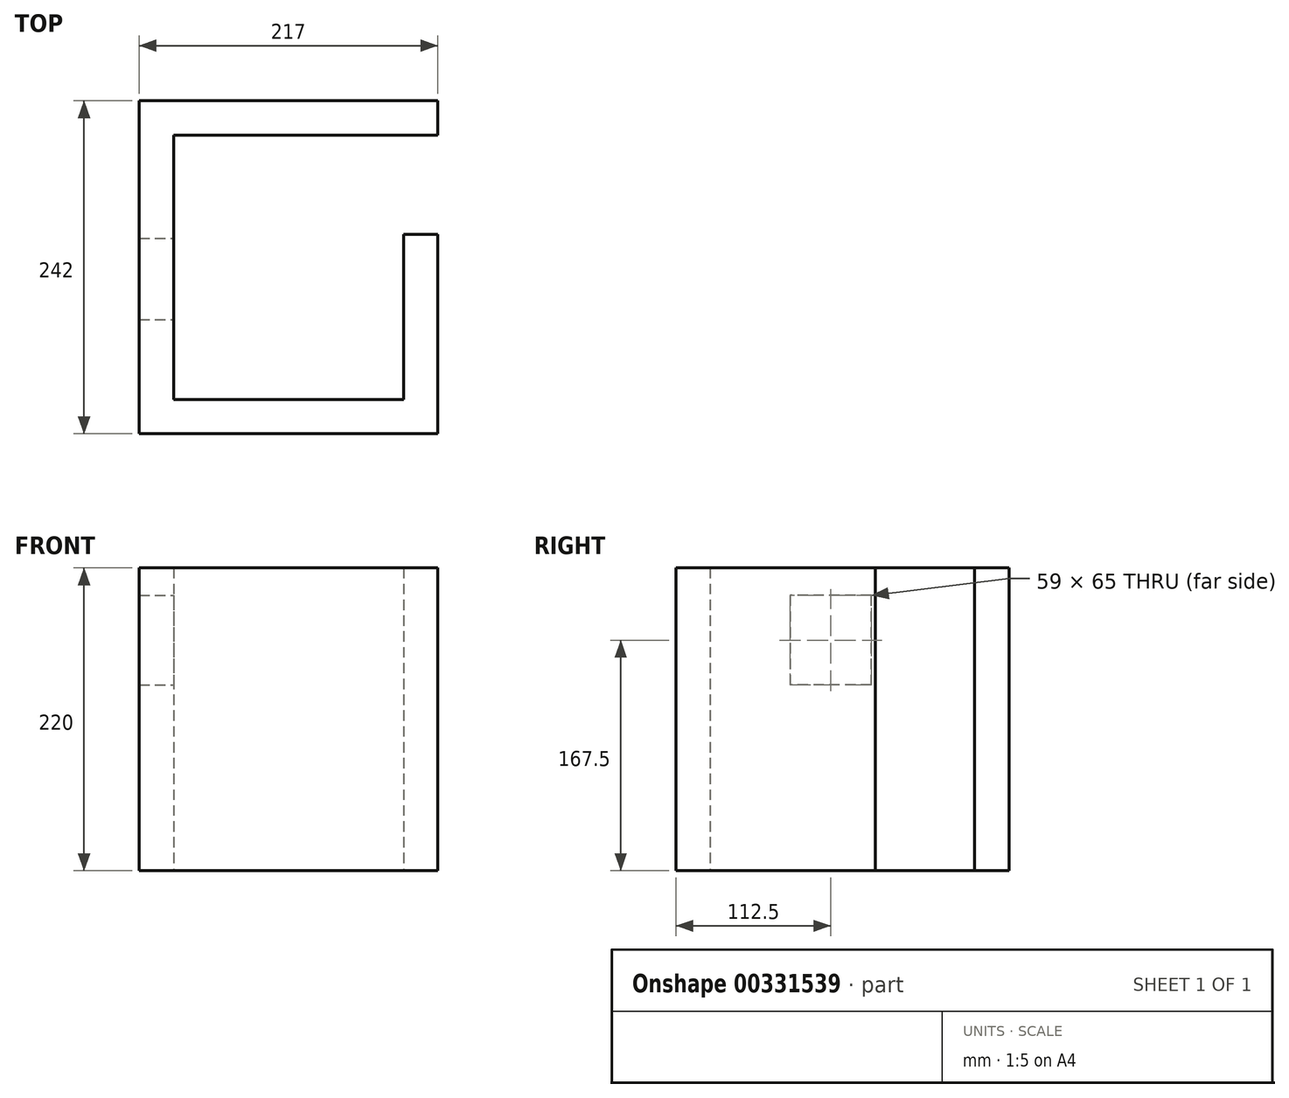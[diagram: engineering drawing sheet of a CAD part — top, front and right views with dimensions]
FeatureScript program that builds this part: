
annotation { "Feature Type Name" : "Feature", "Feature Type Description" : "" }
export const myFeature = defineFeature(function(context is Context, id is Id, definition is map)
    precondition{}
    {
        {
            var Q0;
            Q0=qCreatedBy(makeId("Top.planeOp"),FACE);
            var sketch = newSketch(context, id + "F0", { "sketchPlane" : qUnion([Q0])});
            skLineSegment(sketch, "E0", {"start": v(1313, 440) * mm, "end": v(1313, 406) * mm});
            skLineSegment(sketch, "E1", {"start": v(1313, -267) * mm, "end": v(1313, -301) * mm});
            skLineSegment(sketch, "E2", {"start": v(1313, -301) * mm, "end": v(647, -301) * mm});
            skLineSegment(sketch, "E3", {"start": v(1279, -267) * mm, "end": v(647, -267) * mm});
            skLineSegment(sketch, "E4", {"start": v(1279, 406) * mm, "end": v(688, 406) * mm});
            skLineSegment(sketch, "E5", {"start": v(688, 406) * mm, "end": v(688, -75) * mm});
            skLineSegment(sketch, "E6", {"start": v(688, -75) * mm, "end": v(413, -75) * mm});
            skLineSegment(sketch, "E7", {"start": v(647, -301) * mm, "end": v(647, -267) * mm});
            skLineSegment(sketch, "E8", {"start": v(536, -301) * mm, "end": v(536, -267) * mm});
            skLineSegment(sketch, "E9", {"start": v(536, -267) * mm, "end": v(328, -267) * mm});
            skLineSegment(sketch, "E10", {"start": v(328, -267) * mm, "end": v(328, -407) * mm});
            skLineSegment(sketch, "E11", {"start": v(328, -407) * mm, "end": v(-40, -407) * mm});
            skLineSegment(sketch, "E12", {"start": v(-40, -407) * mm, "end": v(-40, -188) * mm});
            skLineSegment(sketch, "E13", {"start": v(-40, -188) * mm, "end": v(-105, -188) * mm});
            skLineSegment(sketch, "E14", {"start": v(536, -301) * mm, "end": v(362, -301) * mm});
            skLineSegment(sketch, "E15", {"start": v(362, -301) * mm, "end": v(362, -440) * mm});
            skLineSegment(sketch, "E16", {"start": v(-60, -407) * mm, "end": v(-60, -215) * mm});
            skLineSegment(sketch, "E17", {"start": v(-60, -215) * mm, "end": v(-105, -215) * mm});
            skLineSegment(sketch, "E18", {"start": v(-105, -188) * mm, "end": v(-105, -215) * mm});
            skLineSegment(sketch, "E19", {"start": v(-60, -407) * mm, "end": v(-282, -407) * mm});
            skLineSegment(sketch, "E20", {"start": v(-282, -407) * mm, "end": v(-282, -287) * mm});
            skLineSegment(sketch, "E21", {"start": v(-282, -287) * mm, "end": v(-330, -287) * mm});
            skLineSegment(sketch, "E22", {"start": v(-330, -287) * mm, "end": v(-330, -407) * mm});
            skLineSegment(sketch, "E23", {"start": v(-330, -407) * mm, "end": v(-497, -407) * mm});
            skLineSegment(sketch, "E24", {"start": v(-197, -188) * mm, "end": v(-197, -215) * mm});
            skLineSegment(sketch, "E25", {"start": v(-197, -188) * mm, "end": v(-765, -188) * mm});
            skLineSegment(sketch, "E26", {"start": v(-197, -215) * mm, "end": v(-497, -215) * mm});
            skLineSegment(sketch, "E27", {"start": v(-497, -215) * mm, "end": v(-497, -231) * mm});
            skLineSegment(sketch, "E28", {"start": v(-497, -231) * mm, "end": v(-497, -293) * mm});
            skLineSegment(sketch, "E29", {"start": v(-497, -407) * mm, "end": v(-497, -349) * mm});
            skLineSegment(sketch, "E30", {"start": v(413, -75) * mm, "end": v(413, -54) * mm});
            skLineSegment(sketch, "E31", {"start": v(413, -54) * mm, "end": v(667, -54) * mm});
            skLineSegment(sketch, "E32", {"start": v(667, -54) * mm, "end": v(667, 406) * mm});
            skLineSegment(sketch, "E33", {"start": v(667, 406) * mm, "end": v(495, 406) * mm});
            skLineSegment(sketch, "E34", {"start": v(312, 406) * mm, "end": v(391, 406) * mm});
            skLineSegment(sketch, "E35", {"start": v(391, 406) * mm, "end": v(391, 440) * mm});
            skLineSegment(sketch, "E36", {"start": v(495, 406) * mm, "end": v(495, 440) * mm});
            skLineSegment(sketch, "E37", {"start": v(1313, 440) * mm, "end": v(495, 440) * mm});
            skLineSegment(sketch, "E38", {"start": v(312, -75) * mm, "end": v(60, -75) * mm});
            skLineSegment(sketch, "E39", {"start": v(-1279, 406) * mm, "end": v(-1279, 7) * mm});
            skLineSegment(sketch, "E40", {"start": v(-790, 406) * mm, "end": v(-790, 7) * mm});
            skLineSegment(sketch, "E41", {"start": v(-1279, 7) * mm, "end": v(-910, 7) * mm});
            skLineSegment(sketch, "E42", {"start": v(-790, 7) * mm, "end": v(-808, 7) * mm});
            skLineSegment(sketch, "E43", {"start": v(-765, -188) * mm, "end": v(-765, -208) * mm});
            skLineSegment(sketch, "E44", {"start": v(290, 141) * mm, "end": v(290, 406) * mm});
            skLineSegment(sketch, "E45", {"start": v(290, 141) * mm, "end": v(75, 141) * mm});
            skLineSegment(sketch, "E46", {"start": v(75, -46) * mm, "end": v(75, 141) * mm});
            skLineSegment(sketch, "E47", {"start": v(60, -75) * mm, "end": v(60, -46) * mm});
            skLineSegment(sketch, "E48", {"start": v(391, 406) * mm, "end": v(312, 406) * mm});
            skLineSegment(sketch, "E49", {"start": v(-139, 406) * mm, "end": v(-139, 440) * mm});
            skLineSegment(sketch, "E50", {"start": v(-318, 406) * mm, "end": v(-318, 440) * mm});
            skLineSegment(sketch, "E51", {"start": v(-515, 406) * mm, "end": v(-515, 440) * mm});
            skLineSegment(sketch, "E52", {"start": v(-694, 406) * mm, "end": v(-694, 440) * mm});
            skLineSegment(sketch, "E53", {"start": v(-770, 406) * mm, "end": v(-770, 9) * mm});
            skLineSegment(sketch, "E54", {"start": v(-694, 406) * mm, "end": v(-770, 406) * mm});
            skLineSegment(sketch, "E55", {"start": v(75, 406) * mm, "end": v(-139, 406) * mm});
            skLineSegment(sketch, "E56", {"start": v(-318, 406) * mm, "end": v(-515, 406) * mm});
            skLineSegment(sketch, "E57", {"start": v(-318, 440) * mm, "end": v(-515, 440) * mm});
            skLineSegment(sketch, "E58", {"start": v(-770, 9) * mm, "end": v(-754, 9) * mm});
            skLineSegment(sketch, "E59", {"start": v(-677, 9) * mm, "end": v(-659, 9) * mm});
            skLineSegment(sketch, "E60", {"start": v(-659, 9) * mm, "end": v(-659, -5) * mm});
            skLineSegment(sketch, "E61", {"start": v(-659, -5) * mm, "end": v(-659, -46) * mm});
            skLineSegment(sketch, "E62", {"start": v(-659, -46) * mm, "end": v(-60, -46) * mm});
            skLineSegment(sketch, "E63", {"start": v(-60, -75) * mm, "end": v(-60, -46) * mm});
            skLineSegment(sketch, "E64", {"start": v(60, -75) * mm, "end": v(128, -75) * mm});
            skLineSegment(sketch, "E65", {"start": v(60, -46) * mm, "end": v(75, -46) * mm});
            skLineSegment(sketch, "E66", {"start": v(96, -46) * mm, "end": v(290, -46) * mm});
            skLineSegment(sketch, "E67", {"start": v(-60, -75) * mm, "end": v(-677, -75) * mm});
            skLineSegment(sketch, "E68", {"start": v(-677, 9) * mm, "end": v(-677, -75) * mm});
            skLineSegment(sketch, "E69", {"start": v(-754, 9) * mm, "end": v(-754, -13) * mm});
            skLineSegment(sketch, "E70", {"start": v(-808, 7) * mm, "end": v(-808, -13) * mm});
            skLineSegment(sketch, "E71", {"start": v(-808, -13) * mm, "end": v(-754, -13) * mm});
            skLineSegment(sketch, "E72", {"start": v(-910, 7) * mm, "end": v(-910, -29) * mm});
            skLineSegment(sketch, "E73", {"start": v(-1279, -406) * mm, "end": v(-935, -406) * mm});
            skLineSegment(sketch, "E74", {"start": v(-1313, -440) * mm, "end": v(-935, -440) * mm});
            skLineSegment(sketch, "E75", {"start": v(-910, -29) * mm, "end": v(-935, -29) * mm});
            skLineSegment(sketch, "E76", {"start": v(-935, -13) * mm, "end": v(-1279, -13) * mm});
            skLineSegment(sketch, "E77", {"start": v(-910, -132) * mm, "end": v(-935, -132) * mm});
            skLineSegment(sketch, "E78", {"start": v(-910, -29) * mm, "end": v(-910, -13) * mm});
            skLineSegment(sketch, "E79", {"start": v(-935, -406) * mm, "end": v(-935, -132) * mm});
            skLineSegment(sketch, "E80", {"start": v(-935, -29) * mm, "end": v(-935, -13) * mm});
            skLineSegment(sketch, "E81", {"start": v(-877, -208) * mm, "end": v(-877, -188) * mm});
            skLineSegment(sketch, "E82", {"start": v(-910, -132) * mm, "end": v(-910, -188) * mm});
            skLineSegment(sketch, "E83", {"start": v(-877, -188) * mm, "end": v(-910, -188) * mm});
            skLineSegment(sketch, "E84", {"start": v(-877, -208) * mm, "end": v(-904, -208) * mm});
            skLineSegment(sketch, "E85", {"start": v(-904, -208) * mm, "end": v(-904, -406) * mm});
            skLineSegment(sketch, "E86", {"start": v(-904, -406) * mm, "end": v(-648, -406) * mm});
            skLineSegment(sketch, "E87", {"start": v(-765, -208) * mm, "end": v(-648, -208) * mm});
            skLineSegment(sketch, "E88", {"start": v(-648, -208) * mm, "end": v(-648, -273) * mm});
            skLineSegment(sketch, "E89", {"start": v(-648, -406) * mm, "end": v(-648, -343) * mm});
            skLineSegment(sketch, "E90", {"start": v(-935, -440) * mm, "end": v(362, -440) * mm});
            skLineSegment(sketch, "E91", {"start": v(151, 406) * mm, "end": v(151, 440) * mm});
            skLineSegment(sketch, "E92", {"start": v(224, 406) * mm, "end": v(224, 440) * mm});
            skLineSegment(sketch, "E93", {"start": v(290, 406) * mm, "end": v(224, 406) * mm});
            skLineSegment(sketch, "E94", {"start": v(151, 406) * mm, "end": v(96, 406) * mm});
            skLineSegment(sketch, "E95", {"start": v(391, 440) * mm, "end": v(224, 440) * mm});
            skLineSegment(sketch, "E96", {"start": v(151, 440) * mm, "end": v(-139, 440) * mm});
            skLineSegment(sketch, "E97", {"start": v(-907, 406) * mm, "end": v(-907, 440) * mm});
            skLineSegment(sketch, "E98", {"start": v(-1085, 406) * mm, "end": v(-1085, 440) * mm});
            skLineSegment(sketch, "E99", {"start": v(-790, 406) * mm, "end": v(-907, 406) * mm});
            skLineSegment(sketch, "E100", {"start": v(-1085, 406) * mm, "end": v(-1279, 406) * mm});
            skLineSegment(sketch, "E101", {"start": v(-694, 440) * mm, "end": v(-907, 440) * mm});
            skLineSegment(sketch, "E102", {"start": v(-1085, 440) * mm, "end": v(-1313, 440) * mm});
            skLineSegment(sketch, "E103", {"start": v(-1279, -118) * mm, "end": v(-1313, -118) * mm});
            skLineSegment(sketch, "E104", {"start": v(-1279, -297) * mm, "end": v(-1313, -297) * mm});
            skLineSegment(sketch, "E105", {"start": v(-1279, -13) * mm, "end": v(-1279, -118) * mm});
            skLineSegment(sketch, "E106", {"start": v(-1279, -297) * mm, "end": v(-1279, -406) * mm});
            skLineSegment(sketch, "E107", {"start": v(-1313, 440) * mm, "end": v(-1313, -118) * mm});
            skLineSegment(sketch, "E108", {"start": v(-1313, -297) * mm, "end": v(-1313, -440) * mm});
            skLineSegment(sketch, "E109", {"start": v(-648, -273) * mm, "end": v(-630, -273) * mm});
            skLineSegment(sketch, "E110", {"start": v(-648, -343) * mm, "end": v(-630, -343) * mm});
            skLineSegment(sketch, "E111", {"start": v(-515, -349) * mm, "end": v(-497, -349) * mm});
            skLineSegment(sketch, "E112", {"start": v(-515, -293) * mm, "end": v(-497, -293) * mm});
            skLineSegment(sketch, "E113", {"start": v(-515, -349) * mm, "end": v(-515, -406) * mm});
            skLineSegment(sketch, "E114", {"start": v(-630, -343) * mm, "end": v(-630, -406) * mm});
            skLineSegment(sketch, "E115", {"start": v(-630, -406) * mm, "end": v(-515, -406) * mm});
            skLineSegment(sketch, "E116", {"start": v(-630, -273) * mm, "end": v(-630, -206) * mm});
            skLineSegment(sketch, "E117", {"start": v(-630, -206) * mm, "end": v(-515, -206) * mm});
            skLineSegment(sketch, "E118", {"start": v(-515, -293) * mm, "end": v(-515, -206) * mm});
            skLineSegment(sketch, "E119", {"start": v(290, 43) * mm, "end": v(312, 43) * mm});
            skLineSegment(sketch, "E120", {"start": v(290, 124) * mm, "end": v(312, 124) * mm});
            skLineSegment(sketch, "E121", {"start": v(312, -75) * mm, "end": v(312, 43) * mm});
            skLineSegment(sketch, "E122", {"start": v(312, 124) * mm, "end": v(312, 406) * mm});
            skLineSegment(sketch, "E123", {"start": v(290, -46) * mm, "end": v(290, 43) * mm});
            skLineSegment(sketch, "E124", {"start": v(96, 222) * mm, "end": v(75, 222) * mm});
            skLineSegment(sketch, "E125", {"start": v(96, 222) * mm, "end": v(96, 406) * mm});
            skLineSegment(sketch, "E126", {"start": v(75, 222) * mm, "end": v(75, 406) * mm});
            skLineSegment(sketch, "E127", {"start": v(96, -46) * mm, "end": v(96, 124) * mm});
            skLineSegment(sketch, "E128", {"start": v(290, 124) * mm, "end": v(96, 124) * mm});
            skLineSegment(sketch, "E129", {"start": v(1279, -219) * mm, "end": v(1313, -219) * mm});
            skLineSegment(sketch, "E130", {"start": v(1279, -26) * mm, "end": v(1313, -26) * mm});
            skLineSegment(sketch, "E131", {"start": v(1279, 46) * mm, "end": v(1313, 46) * mm});
            skLineSegment(sketch, "E132", {"start": v(1279, 239) * mm, "end": v(1313, 239) * mm});
            skLineSegment(sketch, "E133", {"start": v(1313, 406) * mm, "end": v(1313, 239) * mm});
            skLineSegment(sketch, "E134", {"start": v(1279, 406) * mm, "end": v(1279, 239) * mm});
            skLineSegment(sketch, "E135", {"start": v(1313, 46) * mm, "end": v(1313, -26) * mm});
            skLineSegment(sketch, "E136", {"start": v(1313, -219) * mm, "end": v(1313, -267) * mm});
            skLineSegment(sketch, "E137", {"start": v(1279, 46) * mm, "end": v(1279, -26) * mm});
            skLineSegment(sketch, "E138", {"start": v(1279, -219) * mm, "end": v(1279, -267) * mm});
            skLineSegment(sketch, "E139", {"start": v(1313, -301) * mm, "end": v(1313, 440) * mm});
            skLineSegment(sketch, "E140", {"start": v(1313, -301) * mm, "end": v(362, -301) * mm});
            skLineSegment(sketch, "E141", {"start": v(362, -440) * mm, "end": v(-1313, -440) * mm});
            skLineSegment(sketch, "E142", {"start": v(-1313, 440) * mm, "end": v(-1313, -440) * mm});
            skLineSegment(sketch, "E143", {"start": v(-1313, 440) * mm, "end": v(1313, 440) * mm});
            skLineSegment(sketch, "E144", {"start": v(-321.5, -37.21) * mm, "end": v(-321.5, 162.79) * mm});
            skLineSegment(sketch, "E145", {"start": v(-321.5, -37.21) * mm, "end": v(-511.5, -37.21) * mm});
            skLineSegment(sketch, "E146", {"start": v(-321.5, 162.79) * mm, "end": v(-511.5, 162.79) * mm});
            skLineSegment(sketch, "E147", {"start": v(-511.5, -37.21) * mm, "end": v(-511.5, 162.79) * mm});
            skLineSegment(sketch, "E148", {"start": v(-321.5, -29.2) * mm, "end": v(-511.5, -29.2) * mm});
            skLineSegment(sketch, "E149", {"start": v(-499.08, -21.75) * mm, "end": v(-430.85, -21.75) * mm});
            skLineSegment(sketch, "E150", {"start": v(-430.85, -21.75) * mm, "end": v(-430.85, 2.94) * mm});
            skLineSegment(sketch, "E151", {"start": v(-430.85, 2.94) * mm, "end": v(-499.08, 2.94) * mm});
            skLineSegment(sketch, "E152", {"start": v(-499.08, 2.94) * mm, "end": v(-499.08, -21.75) * mm});
            skLineSegment(sketch, "E153", {"start": v(-333.92, -21.75) * mm, "end": v(-402.15, -21.75) * mm});
            skLineSegment(sketch, "E154", {"start": v(-402.15, -21.75) * mm, "end": v(-402.15, 2.94) * mm});
            skLineSegment(sketch, "E155", {"start": v(-402.15, 2.94) * mm, "end": v(-333.92, 2.94) * mm});
            skLineSegment(sketch, "E156", {"start": v(-333.92, 2.94) * mm, "end": v(-333.92, -21.75) * mm});
            skLineSegment(sketch, "E157", {"start": v(-321.5, 13.1) * mm, "end": v(-416.5, 13.1) * mm});
            skLineSegment(sketch, "E158", {"start": v(-511.5, 36.6) * mm, "end": v(-491.94, 63.04) * mm});
            skLineSegment(sketch, "E159", {"start": v(-491.94, 63.04) * mm, "end": v(-416.5, 13.1) * mm});
            skLineSegment(sketch, "E160", {"start": v(-416.5, 13.1) * mm, "end": v(-511.5, 36.6) * mm});
            skLineSegment(sketch, "E161", {"start": v(-321.5, 159.23) * mm, "end": v(-511.5, 159.23) * mm});
            skLineSegment(sketch, "E162", {"start": v(-552.43, 3.31) * mm, "end": v(-520.43, 3.31) * mm});
            skLineSegment(sketch, "E163", {"start": v(-552.43, 3.31) * mm, "end": v(-552.43, -36.7) * mm});
            skLineSegment(sketch, "E164", {"start": v(-520.43, 3.31) * mm, "end": v(-520.43, -36.7) * mm});
            skLineSegment(sketch, "E165", {"start": v(-552.43, -36.7) * mm, "end": v(-520.43, -36.7) * mm});
            skLineSegment(sketch, "E166", {"start": v(-552.43, -6.69) * mm, "end": v(-520.43, -6.69) * mm});
            skLineSegment(sketch, "E167", {"start": v(-552.43, -3.69) * mm, "end": v(-520.43, -3.69) * mm});
            skLineSegment(sketch, "E168", {"start": v(-552.43, -0.69) * mm, "end": v(-520.43, -0.69) * mm});
            skLineSegment(sketch, "E169", {"start": v(-552.43, 2.31) * mm, "end": v(-520.43, 2.31) * mm});
            skLineSegment(sketch, "E170", {"start": v(-280.57, 3.31) * mm, "end": v(-312.57, 3.31) * mm});
            skLineSegment(sketch, "E171", {"start": v(-280.57, 3.31) * mm, "end": v(-280.57, -36.7) * mm});
            skLineSegment(sketch, "E172", {"start": v(-312.57, 3.31) * mm, "end": v(-312.57, -36.7) * mm});
            skLineSegment(sketch, "E173", {"start": v(-280.57, -36.7) * mm, "end": v(-312.57, -36.7) * mm});
            skLineSegment(sketch, "E174", {"start": v(-280.57, -6.69) * mm, "end": v(-312.57, -6.69) * mm});
            skLineSegment(sketch, "E175", {"start": v(-280.57, -3.69) * mm, "end": v(-312.57, -3.69) * mm});
            skLineSegment(sketch, "E176", {"start": v(-280.57, -0.69) * mm, "end": v(-312.57, -0.69) * mm});
            skLineSegment(sketch, "E177", {"start": v(-280.57, 2.31) * mm, "end": v(-312.57, 2.31) * mm});
            skLineSegment(sketch, "E178", {"start": v(-765, 395.6) * mm, "end": v(-765, 20.6) * mm});
            skLineSegment(sketch, "E179", {"start": v(-765, 395.6) * mm, "end": v(-705, 395.6) * mm});
            skLineSegment(sketch, "E180", {"start": v(-705, 395.6) * mm, "end": v(-705, 20.6) * mm});
            skLineSegment(sketch, "E181", {"start": v(-765, 20.6) * mm, "end": v(-705, 20.6) * mm});
            skLineSegment(sketch, "E182", {"start": v(-705, 395.6) * mm, "end": v(-700, 395.6) * mm});
            skLineSegment(sketch, "E183", {"start": v(-700, 395.6) * mm, "end": v(-700, 20.6) * mm});
            skLineSegment(sketch, "E184", {"start": v(-705, 20.6) * mm, "end": v(-700, 20.6) * mm});
            skLineSegment(sketch, "E185", {"start": v(-705, 114.35) * mm, "end": v(-700, 114.35) * mm});
            skLineSegment(sketch, "E186", {"start": v(-705, 301.85) * mm, "end": v(-700, 301.85) * mm});
            skLineSegment(sketch, "E187", {"start": v(-705, 208.1) * mm, "end": v(-700, 208.1) * mm});
            skLineSegment(sketch, "E188", {"start": v(-705, 348.73) * mm, "end": v(-700, 348.73) * mm});
            skLineSegment(sketch, "E189", {"start": v(-705, 67.47) * mm, "end": v(-700, 67.47) * mm});
            skSolve(sketch);
        }
        {
            var Q0;
            Q0=makeQuery(id+"F0.imprint","IMPRINT",FACE,{"disambiguationData":[TD([[makeQuery(id+"F0.imprint","IMPRINT",EDGE,{"derivedFrom":sQuery(id+"F0.wireOp",EDGE,"E3")}),-1.0]])]});
            var sketch = newSketch(context, id + "F1", { "sketchPlane" : qUnion([Q0])});
            skLineSegment(sketch, "E190.0", {"start": v(-497, -231) * mm, "end": v(-497, -293) * mm});
            skLineSegment(sketch, "E191.0", {"start": v(-330, -215) * mm, "end": v(-497, -215) * mm});
            skLineSegment(sketch, "E192.0", {"start": v(-330, -287) * mm, "end": v(-330, -407) * mm});
            skLineSegment(sketch, "E193.0", {"start": v(-330, -407) * mm, "end": v(-497, -407) * mm});
            skLineSegment(sketch, "E194", {"start": v(-330, -287) * mm, "end": v(-330, -215) * mm});
            skLineSegment(sketch, "E195", {"start": v(-497, -215) * mm, "end": v(-497, -231) * mm});
            skLineSegment(sketch, "E196", {"start": v(-497, -293) * mm, "end": v(-497, -407) * mm});
            skPoint(sketch, "E197.orphan", {"position": v(-197, -215) * mm});
            skSolve(sketch);
        }
        {
            var Q0;
            Q0=qSketchRegion(id+"F1",true);
            extrude(context, id + "F2", {"entities" : qUnion([Q0]), "depth" : 20 * mm});
        }
        {
            var Q0;
            Q0=makeQuery(id+"F0.imprint","IMPRINT",FACE,{"disambiguationData":[TD([[makeQuery(id+"F0.imprint","IMPRINT",EDGE,{"derivedFrom":sQuery(id+"F0.wireOp",EDGE,"E3")}),-1.0]])]});
            var sketch = newSketch(context, id + "F3", { "sketchPlane" : qUnion([Q0])});
            skLineSegment(sketch, "E198.0", {"start": v(-522, -190) * mm, "end": v(-522, -432) * mm});
            skLineSegment(sketch, "E198.1", {"start": v(-305, -190) * mm, "end": v(-522, -190) * mm});
            skLineSegment(sketch, "E198.2", {"start": v(-305, -432) * mm, "end": v(-305, -190) * mm});
            skLineSegment(sketch, "E198.3", {"start": v(-522, -432) * mm, "end": v(-305, -432) * mm});
            skLineSegment(sketch, "E199.0.0", {"start": v(-497, -215) * mm, "end": v(-497, -407) * mm});
            skLineSegment(sketch, "E199.0.1", {"start": v(-497, -407) * mm, "end": v(-330, -407) * mm});
            skLineSegment(sketch, "E199.0.2", {"start": v(-330, -407) * mm, "end": v(-330, -215) * mm});
            skLineSegment(sketch, "E199.0.3", {"start": v(-330, -215) * mm, "end": v(-497, -215) * mm});
            skSolve(sketch);
        }
        {
            var Q0;
            Q0=qSketchRegion(id+"F3",true);
            extrude(context, id + "F4", {"entities" : qUnion([Q0]), "operationType" : NewBodyOperationType.ADD, "depth" : (220 + 20) * mm});
        }
        {
            var Q0;
            Q0=makeQuery(id+"F2.opExtrude","CAP_FACE",FACE,{"disambiguationData":[OSD([sQuery(id+"F1.wireOp",EDGE,"E190.0"),sQuery(id+"F1.wireOp",EDGE,"E191.0"),sQuery(id+"F1.wireOp",EDGE,"E192.0"),sQuery(id+"F1.wireOp",EDGE,"E193.0"),sQuery(id+"F1.wireOp",EDGE,"E194"),sQuery(id+"F1.wireOp",EDGE,"E195"),sQuery(id+"F1.wireOp",EDGE,"E196")])],"isStart":false});
            var sketch = newSketch(context, id + "F5", { "sketchPlane" : qUnion([Q0])});
            skLineSegment(sketch, "E200.0", {"start": v(-282, -287) * mm, "end": v(-330, -287) * mm});
            skLineSegment(sketch, "E201.0", {"start": v(-282, -215) * mm, "end": v(-330, -215) * mm});
            skLineSegment(sketch, "E202", {"start": v(-330, -287) * mm, "end": v(-330, -215) * mm});
            skLineSegment(sketch, "E203", {"start": v(-282, -287) * mm, "end": v(-282, -215) * mm});
            skPoint(sketch, "E204.orphan", {"position": v(-197, -215) * mm});
            skPoint(sketch, "E205.orphan", {"position": v(-497, -215) * mm});
            skSolve(sketch);
        }
        {
            var Q0;
            Q0=qSketchRegion(id+"F5",true);
            extrude(context, id + "F6", {"entities" : qUnion([Q0]), "operationType" : NewBodyOperationType.REMOVE, "depth" : 250 * mm});
        }
        {
            var Q0;
            Q0=makeQuery(id+"F4.opExtrude","SWEPT_FACE",FACE,{"disambiguationData":[OSD([sQuery(id+"F3.wireOp",EDGE,"E199.0.0")])]});
            var sketch = newSketch(context, id + "F7", { "sketchPlane" : qUnion([Q0])});
            skLineSegment(sketch, "E206.0", {"start": v(-407, 0) * mm, "end": v(-349, 0) * mm});
            skLineSegment(sketch, "E207", {"start": v(-270, 220) * mm, "end": v(-349, 220) * mm});
            skLineSegment(sketch, "E208", {"start": v(-349, 220) * mm, "end": v(-349, 135) * mm});
            skLineSegment(sketch, "E209", {"start": v(-349, 135) * mm, "end": v(-270, 135) * mm});
            skLineSegment(sketch, "E210", {"start": v(-270, 135) * mm, "end": v(-270, 220) * mm});
            skSolve(sketch);
        }
        {
            var Q0;
            Q0=qSketchRegion(id+"F7",true);
            extrude(context, id + "F8", {"entities" : qUnion([Q0]), "operationType" : NewBodyOperationType.REMOVE, "oppositeDirection" : true, "depth" : 25 * mm});
        }
        {
            var Q0;
            Q0=makeQuery(id+"F4.opExtrude","SWEPT_FACE",FACE,{"disambiguationData":[OSD([sQuery(id+"F3.wireOp",EDGE,"E199.0.0")])]});
            var sketch = newSketch(context, id + "F9", { "sketchPlane" : qUnion([Q0])});
            skLineSegment(sketch, "E211", {"start": v(-270, 220) * mm, "end": v(-290, 220) * mm});
            skLineSegment(sketch, "E212.0", {"start": v(-270, 135) * mm, "end": v(-270, 220) * mm});
            skLineSegment(sketch, "E213.0", {"start": v(-349, 135) * mm, "end": v(-270, 135) * mm});
            skLineSegment(sketch, "E214", {"start": v(-290, 220) * mm, "end": v(-290, 155) * mm});
            skLineSegment(sketch, "E215", {"start": v(-349, 135) * mm, "end": v(-349, 155) * mm});
            skLineSegment(sketch, "E216", {"start": v(-349, 155) * mm, "end": v(-290, 155) * mm});
            skSolve(sketch);
        }
        {
            var Q0;
            Q0=qSketchRegion(id+"F9",true);
            var Q1;
            Q1=makeQuery(id+"F4.opExtrude","SWEPT_FACE",FACE,{"disambiguationData":[OSD([sQuery(id+"F3.wireOp",EDGE,"E198.0")])]});
            extrude(context, id + "F10", {"entities" : qUnion([Q0]), "operationType" : NewBodyOperationType.ADD, "endBound" : BoundingType.UP_TO_SURFACE, "oppositeDirection" : true, "endBoundEntityFace" : qUnion([Q1]), "depth" : 25 * mm});
        }
        {
            var Q0;
            Q0=makeQuery(id+"F6.boolean.opBoolean","MERGE",FACE,{"derivedFrom":[makeQuery(id+"F2.opExtrude","CAP_FACE",FACE,{"disambiguationData":[OSD([sQuery(id+"F1.wireOp",EDGE,"E190.0"),sQuery(id+"F1.wireOp",EDGE,"E191.0"),sQuery(id+"F1.wireOp",EDGE,"E192.0"),sQuery(id+"F1.wireOp",EDGE,"E193.0"),sQuery(id+"F1.wireOp",EDGE,"E194"),sQuery(id+"F1.wireOp",EDGE,"E195"),sQuery(id+"F1.wireOp",EDGE,"E196")])],"isStart":false}),makeQuery(id+"F6.opExtrude","CAP_FACE",FACE,{"disambiguationData":[OSD([sQuery(id+"F5.wireOp",EDGE,"E200.0"),sQuery(id+"F5.wireOp",EDGE,"E201.0"),sQuery(id+"F5.wireOp",EDGE,"E202"),sQuery(id+"F5.wireOp",EDGE,"E203")])],"isStart":true})]});
            extrude(context, id + "F11", {"entities" : qUnion([Q0]), "operationType" : NewBodyOperationType.REMOVE, "oppositeDirection" : true, "depth" : 25 * mm});
        }
        {
            var Q0;
            Q0=makeQuery(id+"F4.boolean.opBoolean","MERGE",FACE,{"derivedFrom":[makeQuery(id+"F2.opExtrude","CAP_FACE",FACE,{"disambiguationData":[OSD([sQuery(id+"F1.wireOp",EDGE,"E190.0"),sQuery(id+"F1.wireOp",EDGE,"E191.0"),sQuery(id+"F1.wireOp",EDGE,"E192.0"),sQuery(id+"F1.wireOp",EDGE,"E193.0"),sQuery(id+"F1.wireOp",EDGE,"E194"),sQuery(id+"F1.wireOp",EDGE,"E195"),sQuery(id+"F1.wireOp",EDGE,"E196")])],"isStart":true}),makeQuery(id+"F4.opExtrude","CAP_FACE",FACE,{"disambiguationData":[OSD([sQuery(id+"F3.wireOp",EDGE,"E198.0"),sQuery(id+"F3.wireOp",EDGE,"E198.1"),sQuery(id+"F3.wireOp",EDGE,"E198.2"),sQuery(id+"F3.wireOp",EDGE,"E198.3"),sQuery(id+"F3.wireOp",EDGE,"E199.0.0"),sQuery(id+"F3.wireOp",EDGE,"E199.0.1"),sQuery(id+"F3.wireOp",EDGE,"E199.0.2"),sQuery(id+"F3.wireOp",EDGE,"E199.0.3")])],"isStart":true})]});
            extrude(context, id + "F12", {"entities" : qUnion([Q0]), "operationType" : NewBodyOperationType.REMOVE, "oppositeDirection" : true, "depth" : 20 * mm});
        }
    });
